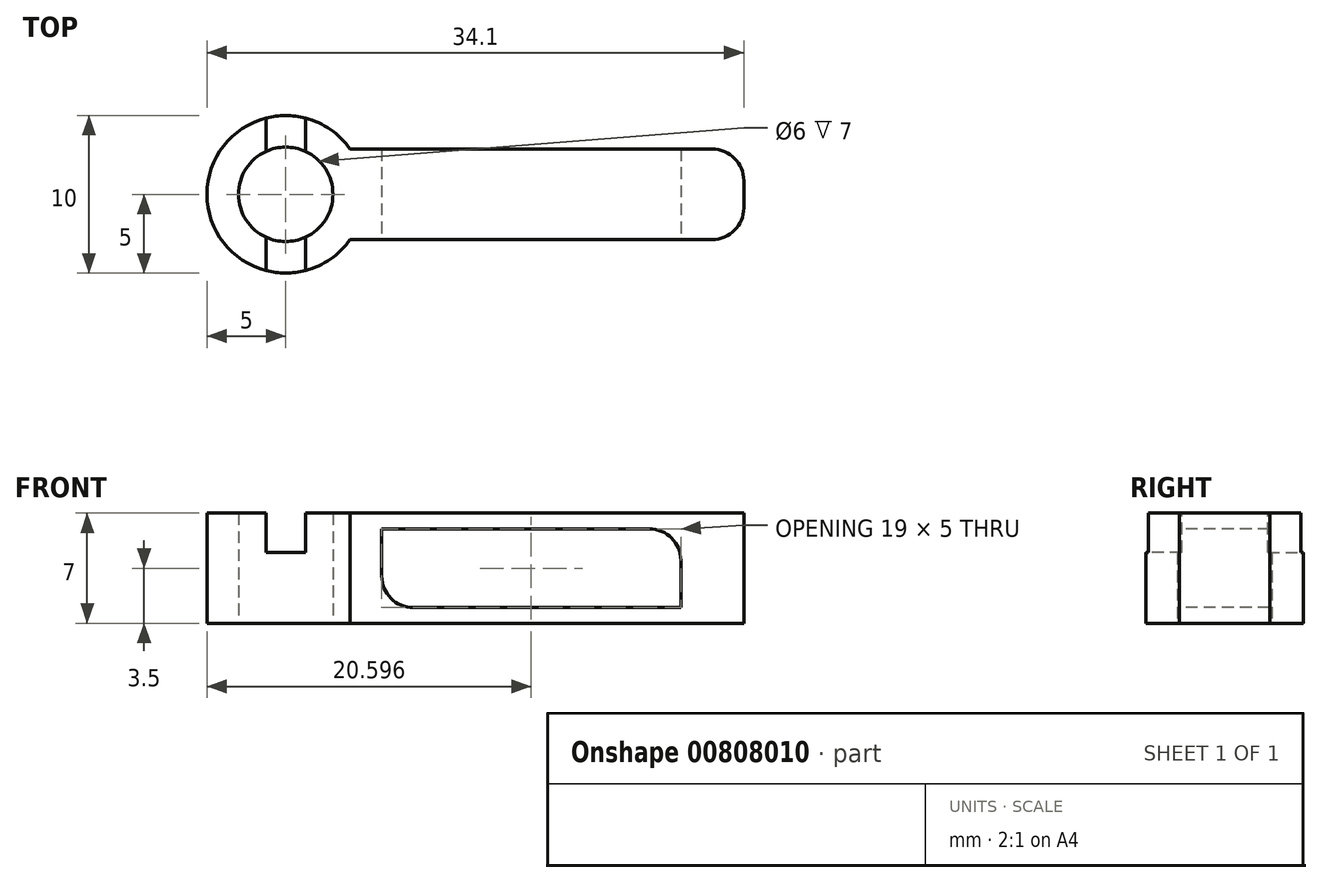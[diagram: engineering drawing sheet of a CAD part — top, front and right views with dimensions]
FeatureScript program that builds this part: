
annotation { "Feature Type Name" : "Feature", "Feature Type Description" : "" }
export const myFeature = defineFeature(function(context is Context, id is Id, definition is map)
    precondition{}
    {
        {
            var Q0;
            Q0=qCreatedBy(makeId("Top.planeOp"),FACE);
            var sketch = newSketch(context, id + "F0", { "sketchPlane" : qUnion([Q0])});
            skCircle(sketch, "E0", {"center": v(0, 0) * mm, "radius": 3 * mm});
            skArc(sketch, "E1", {"start": v(4.1, 2.87) * mm, "mid": v(-5, 0) * mm, "end": v(4.1, -2.87) * mm});
            skLineSegment(sketch, "E2", {"start": v(0, 0) * mm, "end": v(4.1, 2.87) * mm, "construction": true});
            skLineSegment(sketch, "E3", {"start": v(4.1, 2.87) * mm, "end": v(4.1, -2.87) * mm, "construction": true});
            skLineSegment(sketch, "E4", {"start": v(4.1, -2.87) * mm, "end": v(0, 0) * mm, "construction": true});
            skLineSegment(sketch, "E5", {"start": v(4.1, -2.87) * mm, "end": v(27.1, -2.87) * mm});
            skLineSegment(sketch, "E6", {"start": v(4.1, 2.87) * mm, "end": v(27.1, 2.87) * mm});
            skLineSegment(sketch, "E7", {"start": v(29.1, 0.87) * mm, "end": v(29.1, -0.87) * mm});
            skPoint(sketch, "E8.visualSharp", {"position": v(29.1, 2.87) * mm});
            skArc(sketch, "E8.filletArc", {"start": v(29.1, 0.87) * mm, "mid": v(28.5, 2.28) * mm, "end": v(27.1, 2.87) * mm});
            skPoint(sketch, "E9.visualSharp", {"position": v(29.1, -2.87) * mm});
            skArc(sketch, "E9.filletArc", {"start": v(27.1, -2.87) * mm, "mid": v(28.5, -2.28) * mm, "end": v(29.1, -0.87) * mm});
            skSolve(sketch);
        }
        {
            var Q0;
            Q0=makeQuery(id+"F0.imprint","IMPRINT",FACE,{"disambiguationData":[TD([[makeQuery(id+"F0.imprint","IMPRINT",EDGE,{"derivedFrom":sQuery(id+"F0.wireOp",EDGE,"E0")}),-1.0]])]});
            extrude(context, id + "F1", {"entities" : qUnion([Q0]), "depth" : 7 * mm, "offsetDistance" : 25 * mm});
        }
        {
            var Q0;
            Q0=makeQuery(id+"F1.opExtrude","SWEPT_FACE",FACE,{"disambiguationData":[OSD([sQuery(id+"F0.wireOp",EDGE,"E5")])]});
            var sketch = newSketch(context, id + "F2", { "sketchPlane" : qUnion([Q0])});
            skLineSegment(sketch, "E10", {"start": v(4.1, 7) * mm, "end": v(4.1, 6) * mm, "construction": true});
            skLineSegment(sketch, "E11", {"start": v(4.1, 6) * mm, "end": v(6.1, 6) * mm, "construction": true});
            skLineSegment(sketch, "E12", {"start": v(27.1, 0) * mm, "end": v(25.1, 0) * mm, "construction": true});
            skLineSegment(sketch, "E13", {"start": v(25.1, 0) * mm, "end": v(25.1, 1) * mm, "construction": true});
            skLineSegment(sketch, "E14.bottom", {"start": v(6.1, 6) * mm, "end": v(23.1, 6) * mm});
            skLineSegment(sketch, "E14.top", {"start": v(8.1, 1) * mm, "end": v(25.1, 1) * mm});
            skLineSegment(sketch, "E14.left", {"start": v(6.1, 6) * mm, "end": v(6.1, 3) * mm});
            skLineSegment(sketch, "E14.right", {"start": v(25.1, 4) * mm, "end": v(25.1, 1) * mm});
            skPoint(sketch, "E15.visualSharp", {"position": v(6.1, 1) * mm});
            skArc(sketch, "E15.filletArc", {"start": v(6.1, 3) * mm, "mid": v(6.68, 1.59) * mm, "end": v(8.1, 1) * mm});
            skPoint(sketch, "E16.visualSharp", {"position": v(25.1, 6) * mm});
            skArc(sketch, "E16.filletArc", {"start": v(25.1, 4) * mm, "mid": v(24.5, 5.41) * mm, "end": v(23.1, 6) * mm});
            skSolve(sketch);
        }
        {
            var Q0;
            Q0=makeQuery(id+"F2.imprint","IMPRINT",FACE,{"disambiguationData":[TD([[makeQuery(id+"F2.imprint","IMPRINT",EDGE,{"derivedFrom":sQuery(id+"F2.wireOp",EDGE,"E14.bottom")}),-1.0]])]});
            extrude(context, id + "F3", {"entities" : qUnion([Q0]), "operationType" : NewBodyOperationType.REMOVE, "oppositeDirection" : true, "depth" : 25 * mm, "offsetDistance" : 25 * mm});
        }
        {
            var Q0;
            Q0=makeQuery(id+"F1.opExtrude","CAP_FACE",FACE,{"disambiguationData":[OSD([sQuery(id+"F0.wireOp",EDGE,"E0"),sQuery(id+"F0.wireOp",EDGE,"E1"),sQuery(id+"F0.wireOp",EDGE,"E5"),sQuery(id+"F0.wireOp",EDGE,"E6"),sQuery(id+"F0.wireOp",EDGE,"E7"),sQuery(id+"F0.wireOp",EDGE,"E8.filletArc"),sQuery(id+"F0.wireOp",EDGE,"E9.filletArc")])],"isStart":false});
            var sketch = newSketch(context, id + "F4", { "sketchPlane" : qUnion([Q0])});
            skLineSegment(sketch, "E17", {"start": v(0, 0) * mm, "end": v(-1.25, 2.73) * mm, "construction": true});
            skLineSegment(sketch, "E18", {"start": v(-1.25, 2.73) * mm, "end": v(1.25, 2.73) * mm, "construction": true});
            skLineSegment(sketch, "E19", {"start": v(1.25, 2.73) * mm, "end": v(0, 0) * mm, "construction": true});
            skLineSegment(sketch, "E20", {"start": v(-1.25, 2.73) * mm, "end": v(-1.25, 4.84) * mm});
            skLineSegment(sketch, "E21", {"start": v(1.25, 2.73) * mm, "end": v(1.25, 4.84) * mm});
            skLineSegment(sketch, "E22", {"start": v(0, 0) * mm, "end": v(-1.25, -2.73) * mm, "construction": true});
            skLineSegment(sketch, "E23", {"start": v(-1.25, -2.73) * mm, "end": v(-1.25, -4.84) * mm});
            skLineSegment(sketch, "E24", {"start": v(0, 0) * mm, "end": v(1.25, -2.73) * mm, "construction": true});
            skLineSegment(sketch, "E25", {"start": v(1.25, -2.73) * mm, "end": v(1.25, -4.84) * mm});
            skArc(sketch, "E26", {"start": v(-1.25, -2.73) * mm, "mid": v(0, -3) * mm, "end": v(1.25, -2.73) * mm});
            skArc(sketch, "E27", {"start": v(-1.25, -4.84) * mm, "mid": v(0, -5) * mm, "end": v(1.25, -4.84) * mm});
            skArc(sketch, "E28.trimOffspring", {"start": v(1.25, 4.84) * mm, "mid": v(0, 5) * mm, "end": v(-1.25, 4.84) * mm});
            skArc(sketch, "E29.trimOffspring", {"start": v(1.25, 2.73) * mm, "mid": v(0, 3) * mm, "end": v(-1.25, 2.73) * mm});
            skSolve(sketch);
        }
        {
            var Q0;
            Q0=makeQuery(id+"F4.imprint","IMPRINT",FACE,{"disambiguationData":[TD([[makeQuery(id+"F4.imprint","IMPRINT",EDGE,{"derivedFrom":sQuery(id+"F4.wireOp",EDGE,"E20")}),-1.0]])]});
            var Q1;
            Q1=makeQuery(id+"F4.imprint","IMPRINT",FACE,{"disambiguationData":[TD([[makeQuery(id+"F4.imprint","IMPRINT",EDGE,{"derivedFrom":sQuery(id+"F4.wireOp",EDGE,"E23")}),1.0]])]});
            extrude(context, id + "F5", {"entities" : qUnion([Q0, Q1]), "operationType" : NewBodyOperationType.REMOVE, "oppositeDirection" : true, "depth" : 2.5 * mm, "offsetDistance" : 25 * mm});
        }
    });
